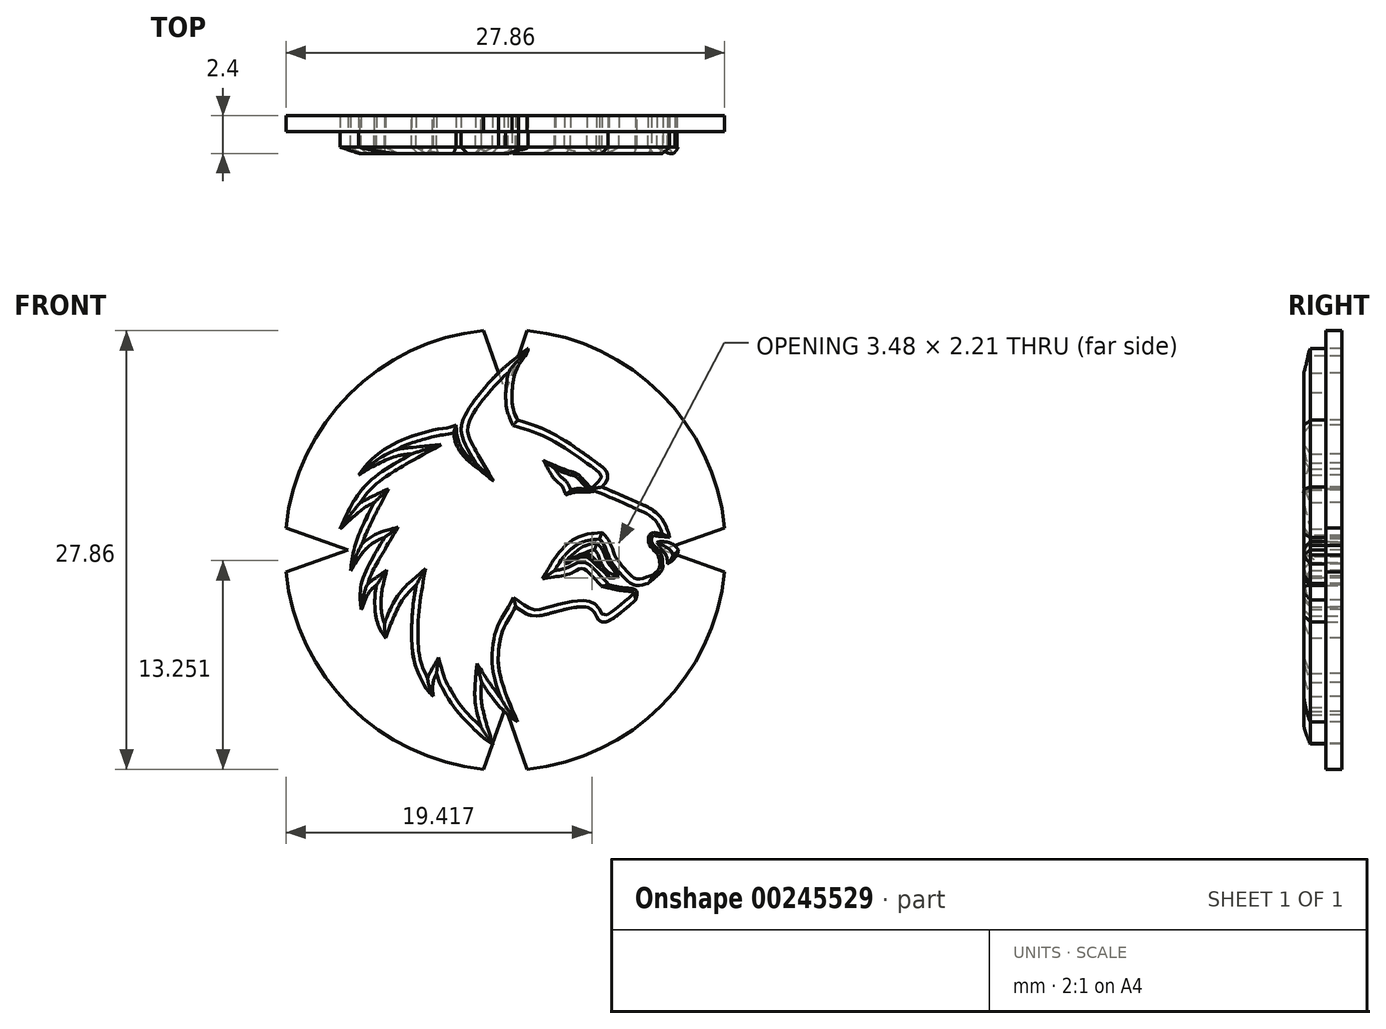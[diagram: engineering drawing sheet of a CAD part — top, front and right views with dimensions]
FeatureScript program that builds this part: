
annotation { "Feature Type Name" : "Feature", "Feature Type Description" : "" }
export const myFeature = defineFeature(function(context is Context, id is Id, definition is map)
    precondition{}
    {
        {
            var Q0;
            Q0=qCreatedBy(makeId("Front.planeOp"),FACE);
            var sketch = newSketch(context, id + "F0", { "sketchPlane" : qUnion([Q0])});
            skCircle(sketch, "E0", {"center": v(0, 0) * mm, "radius": 18 * mm, "construction": true});
            skCircle(sketch, "E1", {"center": v(0, 0) * mm, "radius": 17 * mm, "construction": true});
            skCircle(sketch, "E2", {"center": v(0, 0) * mm, "radius": 15 * mm, "construction": true});
            skLineSegment(sketch, "E3", {"start": v(-18, 18) * mm, "end": v(-18, -18) * mm, "construction": true});
            skLineSegment(sketch, "E4", {"start": v(-18, -18) * mm, "end": v(18, -18) * mm, "construction": true});
            skLineSegment(sketch, "E5", {"start": v(18, -18) * mm, "end": v(18, 18) * mm, "construction": true});
            skLineSegment(sketch, "E6", {"start": v(18, 18) * mm, "end": v(-18, 18) * mm, "construction": true});
            skFitSpline(sketch, "E7", {"points": [v(-10.49, 1.33) * mm, v(-9.43, 3.4) * mm, v(-8.08, 4.8) * mm, v(-5.95, 6.1) * mm], "startDerivative": vector(2.88, 6.53) * mm, "endDerivative": vector(6.47, 3.62) * mm});
            skFitSpline(sketch, "E8", {"points": [v(-9.32, 4.76) * mm, v(-8.35, 5.34) * mm, v(-6.9, 5.95) * mm, v(-5.95, 6.1) * mm], "startDerivative": vector(2.77, 1.79) * mm, "endDerivative": vector(3.02, 0.29) * mm});
            skFitSpline(sketch, "E9", {"points": [v(-3.13, 7.94) * mm, v(-3.48, 7.8) * mm, v(-4.26, 7.67) * mm, v(-5.45, 7.37) * mm, v(-6.65, 6.94) * mm, v(-7.65, 6.4) * mm, v(-8.6, 5.63) * mm, v(-9.32, 4.76) * mm], "startDerivative": vector(-3.58, -1.84) * mm, "endDerivative": vector(-4.37, -5.9) * mm});
            skFitSpline(sketch, "E10", {"points": [v(-1.9, 5.53) * mm, v(-2.35, 5.92) * mm, v(-2.78, 6.48) * mm, v(-3.04, 7.1) * mm, v(-3.13, 7.94) * mm], "startDerivative": vector(-1.97, 1.54) * mm, "endDerivative": vector(-0.18, 3.2) * mm});
            skFitSpline(sketch, "E11", {"points": [v(-8.33, 3.01) * mm, v(-8.87, 2.72) * mm, v(-9.58, 2.16) * mm, v(-10.49, 1.33) * mm], "startDerivative": vector(-1.95, -0.93) * mm, "endDerivative": vector(-2.37, -2.22) * mm});
            skFitSpline(sketch, "E12", {"points": [v(-9.83, -1.31) * mm, v(-9.69, -0.31) * mm, v(-9.39, 0.77) * mm, v(-8.9, 1.88) * mm, v(-8.33, 3.01) * mm], "startDerivative": vector(0.5, 4.23) * mm, "endDerivative": vector(2.2, 4.32) * mm});
            skFitSpline(sketch, "E13", {"points": [v(-7.67, 0.79) * mm, v(-8.05, 0.65) * mm, v(-8.65, 0.25) * mm, v(-9.12, -0.25) * mm, v(-9.83, -1.31) * mm], "startDerivative": vector(-1.94, -0.57) * mm, "endDerivative": vector(-2.32, -3.56) * mm});
            skFitSpline(sketch, "E14", {"points": [v(-9.15, -3.8) * mm, v(-9.22, -3.06) * mm, v(-9.1, -2) * mm, v(-8.5, -0.63) * mm, v(-7.67, 0.79) * mm], "startDerivative": vector(-0.5, 3.6) * mm, "endDerivative": vector(2.91, 4.84) * mm});
            skFitSpline(sketch, "E15", {"points": [v(-8.17, -2.23) * mm, v(-8.56, -2.55) * mm, v(-8.86, -3.09) * mm, v(-9.15, -3.8) * mm], "startDerivative": vector(-1.36, -0.97) * mm, "endDerivative": vector(-0.78, -1.96) * mm});
            skFitSpline(sketch, "E16", {"points": [v(-7.6, -5.6) * mm, v(-7.87, -5.2) * mm, v(-8.15, -4.51) * mm, v(-8.29, -3.61) * mm, v(-8.26, -2.67) * mm, v(-8.17, -2.23) * mm], "startDerivative": vector(-1.6, 2.21) * mm, "endDerivative": vector(0.59, 2.45) * mm});
            skFitSpline(sketch, "E17", {"points": [v(-5.66, -2.23) * mm, v(-6.13, -2.67) * mm, v(-6.67, -3.42) * mm, v(-7.18, -4.48) * mm, v(-7.6, -5.6) * mm], "startDerivative": vector(-2.28, -2) * mm, "endDerivative": vector(-1.47, -4.03) * mm});
            skFitSpline(sketch, "E18", {"points": [v(-4.57, -9.32) * mm, v(-4.99, -8.85) * mm, v(-5.45, -8.01) * mm, v(-5.86, -6.73) * mm, v(-5.95, -4.95) * mm, v(-5.86, -3.52) * mm, v(-5.66, -2.23) * mm], "startDerivative": vector(-3.52, 3.53) * mm, "endDerivative": vector(1.32, 7.43) * mm});
            skFitSpline(sketch, "E19", {"points": [v(-4.37, -7.85) * mm, v(-4.52, -8.18) * mm, v(-4.62, -8.75) * mm, v(-4.57, -9.32) * mm], "startDerivative": vector(-0.58, -1.04) * mm, "endDerivative": vector(0.22, -1.55) * mm});
            skFitSpline(sketch, "E20", {"points": [v(-0.79, -12.36) * mm, v(-1.46, -11.87) * mm, v(-2.24, -11.13) * mm, v(-3.13, -10.15) * mm, v(-3.75, -9.22) * mm, v(-4.15, -8.49) * mm, v(-4.37, -7.85) * mm], "startDerivative": vector(-4.36, 2.91) * mm, "endDerivative": vector(-1.35, 4.54) * mm});
            skFitSpline(sketch, "E21", {"points": [v(-1.51, -8.4) * mm, v(-1.54, -8.88) * mm, v(-1.52, -9.6) * mm, v(-1.37, -10.41) * mm, v(-1.1, -11.41) * mm, v(-0.79, -12.36) * mm], "startDerivative": vector(-0.24, -2.87) * mm, "endDerivative": vector(1.38, -4.16) * mm});
            skFitSpline(sketch, "E22", {"points": [v(0.78, -10.93) * mm, v(0.3, -10.6) * mm, v(-0.3, -10.03) * mm, v(-0.96, -9.22) * mm, v(-1.51, -8.4) * mm], "startDerivative": vector(-2.26, 1.48) * mm, "endDerivative": vector(-1.97, 3) * mm});
            skFitSpline(sketch, "E23", {"points": [v(0.66, -3.6) * mm, v(0.38, -4.1) * mm, v(-0.17, -5.12) * mm, v(-0.42, -6.39) * mm, v(-0.42, -7.5) * mm, v(0.07, -9.25) * mm, v(0.78, -10.93) * mm], "startDerivative": vector(-2.16, -4.03) * mm, "endDerivative": vector(3.61, -8.1) * mm});
            skFitSpline(sketch, "E24", {"points": [v(8.27, -3.19) * mm, v(6.84, -4.35) * mm, v(6.29, -4.58) * mm, v(5.92, -4.45) * mm, v(5.68, -4.04) * mm, v(5.38, -3.71) * mm, v(4.74, -3.62) * mm, v(3.17, -3.93) * mm, v(2.23, -4.17) * mm, v(1.52, -4.14) * mm, v(0.66, -3.6) * mm], "startDerivative": vector(-10.5, -9.12) * mm, "endDerivative": vector(-7.73, 5.86) * mm});
            skFitSpline(sketch, "E25", {"points": [v(6.58, -2.23) * mm, v(7.37, -2.39) * mm, v(8, -2.46) * mm, v(8.33, -2.62) * mm, v(8.27, -3.19) * mm], "startDerivative": vector(2.74, -0.65) * mm, "endDerivative": vector(-0.75, -2.68) * mm});
            skFitSpline(sketch, "E26", {"points": [v(3.13, -1.31) * mm, v(3.95, -1.14) * mm, v(4.38, -0.92) * mm, v(4.8, -0.78) * mm, v(5.26, -0.9) * mm, v(5.73, -1.31) * mm, v(6.58, -2.23) * mm], "startDerivative": vector(4.8, 0.73) * mm, "endDerivative": vector(3.99, -4.35) * mm});
            skFitSpline(sketch, "E27", {"points": [v(1.45, 12.8) * mm, v(0.94, 12.41) * mm, v(-0.34, 11.34) * mm, v(-1.27, 10.36) * mm, v(-2.2, 9.16) * mm, v(-2.7, 8.25) * mm, v(-2.8, 7.58) * mm, v(-2.59, 6.8) * mm, v(-1.9, 5.53) * mm], "startDerivative": vector(-4.66, -3.44) * mm, "endDerivative": vector(5.45, -9.26) * mm});
            skFitSpline(sketch, "E28", {"points": [v(0.78, 8.24) * mm, v(0.5, 8.98) * mm, v(0.43, 10.17) * mm, v(0.78, 11.63) * mm, v(1.38, 12.53) * mm, v(1.45, 12.8) * mm], "startDerivative": vector(-1.77, 3.71) * mm, "endDerivative": vector(0.21, 2.22) * mm});
            skFitSpline(sketch, "E29", {"points": [v(6.13, 4) * mm, v(6.43, 4.36) * mm, v(6.47, 4.88) * mm, v(5.82, 5.53) * mm, v(4.55, 6.42) * mm, v(3.45, 7.14) * mm, v(2.33, 7.72) * mm, v(0.78, 8.24) * mm], "startDerivative": vector(3.54, 3.42) * mm, "endDerivative": vector(-9.1, 2.77) * mm});
            skFitSpline(sketch, "E30", {"points": [v(3.18, 5.13) * mm, v(3.42, 4.76) * mm, v(3.68, 4.52) * mm, v(3.89, 4.32) * mm, v(4.03, 4.1) * mm, v(4.15, 3.8) * mm], "startDerivative": vector(0.95, -1.73) * mm, "endDerivative": vector(0.59, -1.54) * mm});
            skFitSpline(sketch, "E31", {"points": [v(5.2, 3.89) * mm, v(4.98, 4.14) * mm, v(4.79, 4.36) * mm, v(4.61, 4.53) * mm, v(4.4, 4.7) * mm, v(4.19, 4.76) * mm, v(3.81, 4.89) * mm, v(3.5, 5) * mm, v(3.18, 5.13) * mm], "startDerivative": vector(-1.64, 1.95) * mm, "endDerivative": vector(-2.38, 1.04) * mm});
            skFitSpline(sketch, "E32", {"points": [v(4.15, 3.8) * mm, v(4.4, 3.87) * mm, v(4.62, 3.9) * mm, v(4.85, 3.89) * mm, v(5.2, 3.89) * mm], "startDerivative": vector(1, 0.29) * mm, "endDerivative": vector(1.25, 0.03) * mm});
            skFitSpline(sketch, "E33", {"points": [v(10.44, 0.79) * mm, v(10.33, 1.18) * mm, v(10, 1.9) * mm, v(9.66, 2.29) * mm, v(9.23, 2.62) * mm, v(8.4, 3.01) * mm, v(7.17, 3.55) * mm, v(6.13, 4) * mm], "startDerivative": vector(-0.8, 3.45) * mm, "endDerivative": vector(-5.9, 2.46) * mm});
            skFitSpline(sketch, "E34", {"points": [v(3.13, -1.31) * mm, v(3.31, -1) * mm, v(3.74, -0.39) * mm, v(4.35, 0.19) * mm, v(5.03, 0.54) * mm, v(5.97, 0.69) * mm], "startDerivative": vector(1.16, 2.03) * mm, "endDerivative": vector(4.3, 0.39) * mm});
            skFitSpline(sketch, "E35", {"points": [v(9.07, -2.12) * mm, v(8.67, -2.23) * mm, v(8.18, -2.23) * mm, v(7.78, -1.97) * mm, v(7.35, -1.56) * mm, v(6.85, -0.93) * mm, v(6.64, -0.63) * mm, v(6.53, -0.35) * mm, v(6.34, 0.14) * mm, v(6.2, 0.43) * mm, v(5.97, 0.69) * mm], "startDerivative": vector(-3.96, -1.23) * mm, "endDerivative": vector(-2.8, 2.95) * mm});
            skFitSpline(sketch, "E36", {"points": [v(9.07, -2.12) * mm, v(9.38, -1.86) * mm, v(9.75, -1.5) * mm, v(9.96, -1.27) * mm, v(10, -0.95) * mm, v(9.93, -0.42) * mm, v(9.72, -0.05) * mm, v(9.5, 0.22) * mm, v(9.32, 0.44) * mm, v(9.27, 0.63) * mm, v(9.29, 0.79) * mm, v(9.37, 0.9) * mm, v(9.6, 0.89) * mm, v(10.44, 0.79) * mm], "startDerivative": vector(3.69, 2.83) * mm, "endDerivative": vector(7.96, -0.84) * mm});
            skFitSpline(sketch, "E37", {"points": [v(5.8, 0.43) * mm, v(5.97, 0.27) * mm, v(6.17, 0) * mm, v(6.34, -0.42) * mm, v(6.51, -0.77) * mm, v(6.8, -1.2) * mm, v(7.23, -1.64) * mm], "startDerivative": vector(1.64, -1.22) * mm, "endDerivative": vector(2.15, -2.15) * mm});
            skFitSpline(sketch, "E38", {"points": [v(6.58, -1.77) * mm, v(6.9, -1.77) * mm, v(7.23, -1.64) * mm], "startDerivative": vector(0.65, -0.06) * mm, "endDerivative": vector(0.64, 0.33) * mm});
            skFitSpline(sketch, "E39", {"points": [v(9.62, 0.48) * mm, v(9.82, 0.2) * mm, v(9.98, -0.06) * mm, v(10.12, -0.22) * mm, v(10.22, -0.37) * mm, v(10.28, -0.58) * mm, v(10.28, -0.88) * mm], "startDerivative": vector(1.09, -1.48) * mm, "endDerivative": vector(-0.04, -1.75) * mm});
            skFitSpline(sketch, "E40", {"points": [v(9.62, 0.48) * mm, v(9.76, 0.52) * mm, v(10.17, 0.5) * mm, v(10.65, 0.36) * mm, v(10.98, 0) * mm], "startDerivative": vector(0.77, 0.28) * mm, "endDerivative": vector(1.05, -1.4) * mm});
            skFitSpline(sketch, "E41", {"points": [v(10.28, -0.88) * mm, v(10.47, -0.78) * mm, v(10.7, -0.6) * mm, v(10.86, -0.37) * mm, v(10.95, -0.21) * mm, v(10.98, 0) * mm], "startDerivative": vector(0.96, 0.5) * mm, "endDerivative": vector(0.12, 1.19) * mm});
            skFitSpline(sketch, "E42", {"points": [v(3.75, -0.86) * mm, v(3.94, -0.84) * mm, v(4.22, -0.68) * mm, v(4.57, -0.52) * mm, v(4.9, -0.44) * mm, v(5.23, -0.49) * mm, v(5.51, -0.71) * mm, v(5.9, -1.07) * mm, v(6.2, -1.33) * mm, v(6.44, -1.6) * mm, v(6.58, -1.77) * mm], "startDerivative": vector(2.52, -0.03) * mm, "endDerivative": vector(1.67, -2) * mm});
            skFitSpline(sketch, "E43", {"points": [v(5.8, 0.43) * mm, v(5.46, 0.38) * mm, v(5.16, 0.29) * mm, v(4.77, 0.11) * mm, v(4.34, -0.23) * mm, v(3.98, -0.55) * mm, v(3.75, -0.86) * mm], "startDerivative": vector(-2.27, -0.23) * mm, "endDerivative": vector(-1.33, -1.97) * mm});
            skSolve(sketch);
        }
        {
            var Q0;
            Q0=qCreatedBy(makeId("Front.planeOp"),FACE);
            var sketch = newSketch(context, id + "F1", { "sketchPlane" : qUnion([Q0])});
            skCircle(sketch, "E44", {"center": v(0, 0) * mm, "radius": 20 * mm});
            skLineSegment(sketch, "E45", {"start": v(0, 25.78) * mm, "end": v(0, -27.28) * mm, "construction": true});
            skLineSegment(sketch, "E46", {"start": v(-28.3, 0) * mm, "end": v(31.37, 0) * mm, "construction": true});
            skLineSegment(sketch, "E47", {"start": v(-22, 0) * mm, "end": v(-16, 2.12) * mm});
            skLineSegment(sketch, "E48", {"start": v(-16, 2.12) * mm, "end": v(-10, 0) * mm});
            skLineSegment(sketch, "E49", {"start": v(-10, 0) * mm, "end": v(-16, -2.12) * mm});
            skLineSegment(sketch, "E50", {"start": v(-16, -2.12) * mm, "end": v(-22, 0) * mm});
            skLineSegment(sketch, "E51.0", {"start": v(-16, 1.06) * mm, "end": v(-13, 0) * mm});
            skLineSegment(sketch, "E51.1", {"start": v(-19, 0) * mm, "end": v(-16, 1.06) * mm});
            skLineSegment(sketch, "E51.2", {"start": v(-16, -1.06) * mm, "end": v(-19, 0) * mm});
            skLineSegment(sketch, "E51.3", {"start": v(-13, 0) * mm, "end": v(-16, -1.06) * mm});
            skCircle(sketch, "E52", {"center": v(0, 0) * mm, "radius": 14 * mm});
            skLineSegment(sketch, "E53", {"start": v(-23.43, 23.43) * mm, "end": v(21.13, -21.13) * mm, "construction": true});
            skLineSegment(sketch, "E54.MirrorCS", {"start": v(10, 0) * mm, "end": v(16, -2.12) * mm});
            skLineSegment(sketch, "E55.MirrorCS", {"start": v(13, 0) * mm, "end": v(16, -1.06) * mm});
            skLineSegment(sketch, "E56.MirrorCS", {"start": v(16, -1.06) * mm, "end": v(19, 0) * mm});
            skLineSegment(sketch, "E57.MirrorCS", {"start": v(16, -2.12) * mm, "end": v(22, 0) * mm});
            skLineSegment(sketch, "E58.MirrorCS", {"start": v(22, 0) * mm, "end": v(16, 2.12) * mm});
            skLineSegment(sketch, "E59.MirrorCS", {"start": v(16, 2.12) * mm, "end": v(10, 0) * mm});
            skLineSegment(sketch, "E60.MirrorCS", {"start": v(16, 1.06) * mm, "end": v(13, 0) * mm});
            skLineSegment(sketch, "E61.MirrorCS", {"start": v(19, 0) * mm, "end": v(16, 1.06) * mm});
            skLineSegment(sketch, "E62.MirrorCS", {"start": v(0, 19) * mm, "end": v(-1.06, 16) * mm});
            skLineSegment(sketch, "E63.MirrorCS", {"start": v(1.06, 16) * mm, "end": v(0, 19) * mm});
            skLineSegment(sketch, "E64.MirrorCS", {"start": v(0, 22) * mm, "end": v(-2.12, 16) * mm});
            skLineSegment(sketch, "E65.MirrorCS", {"start": v(2.12, 16) * mm, "end": v(0, 22) * mm});
            skLineSegment(sketch, "E66.MirrorCS", {"start": v(0, 10) * mm, "end": v(2.12, 16) * mm});
            skLineSegment(sketch, "E67.MirrorCS", {"start": v(0, 13) * mm, "end": v(1.06, 16) * mm});
            skLineSegment(sketch, "E68.MirrorCS", {"start": v(-1.06, 16) * mm, "end": v(0, 13) * mm});
            skLineSegment(sketch, "E69.MirrorCS", {"start": v(-2.12, 16) * mm, "end": v(0, 10) * mm});
            skLineSegment(sketch, "E70.MirrorCS", {"start": v(0, -10) * mm, "end": v(2.12, -16) * mm});
            skLineSegment(sketch, "E71.MirrorCS", {"start": v(0, -13) * mm, "end": v(1.06, -16) * mm});
            skLineSegment(sketch, "E72.MirrorCS", {"start": v(-1.06, -16) * mm, "end": v(0, -13) * mm});
            skLineSegment(sketch, "E73.MirrorCS", {"start": v(-2.12, -16) * mm, "end": v(0, -10) * mm});
            skLineSegment(sketch, "E74.MirrorCS", {"start": v(0, -22) * mm, "end": v(-2.12, -16) * mm});
            skLineSegment(sketch, "E75.MirrorCS", {"start": v(0, -19) * mm, "end": v(-1.06, -16) * mm});
            skLineSegment(sketch, "E76.MirrorCS", {"start": v(1.06, -16) * mm, "end": v(0, -19) * mm});
            skLineSegment(sketch, "E77.MirrorCS", {"start": v(2.12, -16) * mm, "end": v(0, -22) * mm});
            skSolve(sketch);
        }
        {
            var Q0;
            {var subQ12=sQuery(id+"F1.wireOp",EDGE,"E48");var subQ14=sQuery(id+"F1.wireOp",EDGE,"E49");var subQ18=makeQuery(id+"F1.imprint","INTERSECT",VERTEX,{"derivedFrom":[subQ12,subQ14]});Q0=makeQuery(id+"F1.imprint","IMPRINT",FACE,{"disambiguationData":[TD([[makeQuery(id+"F1.imprint","IMPRINT",EDGE,{"disambiguationData":[TD([[subQ18,1.0]])],"derivedFrom":subQ12}),1.0]])]});}
            extrude(context, id + "F2", {"entities" : qUnion([Q0]), "oppositeDirection" : true, "depth" : 1 * mm});
        }
        {
            var Q0;
            Q0=makeQuery(id+"F0.imprint","IMPRINT",FACE,{"disambiguationData":[TD([[makeQuery(id+"F0.imprint","IMPRINT",EDGE,{"derivedFrom":sQuery(id+"F0.wireOp",EDGE,"E7")}),-1.0]])]});
            var Q1;
            Q1=makeQuery(id+"F0.imprint","IMPRINT",FACE,{"disambiguationData":[TD([[makeQuery(id+"F0.imprint","IMPRINT",EDGE,{"derivedFrom":sQuery(id+"F0.wireOp",EDGE,"e38c4cf1-d7ad-4980-8dd1-fedaf0ec52b0")}),-1.0]])]});
            var Q2;
            Q2=makeQuery(id+"F0.imprint","IMPRINT",FACE,{"disambiguationData":[TD([[makeQuery(id+"F0.imprint","IMPRINT",EDGE,{"derivedFrom":sQuery(id+"F0.wireOp",EDGE,"E39")}),1.0]])]});
            var Q3;
            Q3=makeQuery(id+"F0.imprint","IMPRINT",FACE,{"disambiguationData":[TD([[makeQuery(id+"F0.imprint","IMPRINT",EDGE,{"derivedFrom":sQuery(id+"F0.wireOp",EDGE,"E37")}),-1.0]])]});
            extrude(context, id + "F3", {"entities" : qUnion([Q0, Q1, Q2, Q3]), "operationType" : NewBodyOperationType.REMOVE, "oppositeDirection" : true, "depth" : 1 * mm});
        }
        {
            var Q0;
            Q0 = qSketchRegion(id + "F0", true);
            extrude(context, id + "F4", {"entities" : qUnion([Q0]), "depth" : 1.4 * mm});
        }
        {
            var Q0;
            Q0=makeQuery(id+"F4.opExtrude","CAP_EDGE",EDGE,{"disambiguationData":[OSD([sQuery(id+"F0.wireOp",EDGE,"E23")])],"isStart":false});
            var Q1;
            Q1=makeQuery(id+"F4.opExtrude","CAP_EDGE",EDGE,{"disambiguationData":[OSD([sQuery(id+"F0.wireOp",EDGE,"E24")])],"isStart":false});
            var Q2;
            Q2=makeQuery(id+"F4.opExtrude","CAP_EDGE",EDGE,{"disambiguationData":[OSD([sQuery(id+"F0.wireOp",EDGE,"E22")])],"isStart":false});
            var Q3;
            Q3=makeQuery(id+"F4.opExtrude","CAP_EDGE",EDGE,{"disambiguationData":[OSD([sQuery(id+"F0.wireOp",EDGE,"E21")])],"isStart":false});
            var Q4;
            Q4=makeQuery(id+"F4.opExtrude","CAP_EDGE",EDGE,{"disambiguationData":[OSD([sQuery(id+"F0.wireOp",EDGE,"E20")])],"isStart":false});
            var Q5;
            Q5=makeQuery(id+"F4.opExtrude","CAP_EDGE",EDGE,{"disambiguationData":[OSD([sQuery(id+"F0.wireOp",EDGE,"E19")])],"isStart":false});
            var Q6;
            Q6=makeQuery(id+"F4.opExtrude","CAP_EDGE",EDGE,{"disambiguationData":[OSD([sQuery(id+"F0.wireOp",EDGE,"E18")])],"isStart":false});
            var Q7;
            Q7=makeQuery(id+"F4.opExtrude","CAP_EDGE",EDGE,{"disambiguationData":[OSD([sQuery(id+"F0.wireOp",EDGE,"E17")])],"isStart":false});
            var Q8;
            Q8=makeQuery(id+"F4.opExtrude","CAP_EDGE",EDGE,{"disambiguationData":[OSD([sQuery(id+"F0.wireOp",EDGE,"E16")])],"isStart":false});
            var Q9;
            Q9=makeQuery(id+"F4.opExtrude","CAP_EDGE",EDGE,{"disambiguationData":[OSD([sQuery(id+"F0.wireOp",EDGE,"E15")])],"isStart":false});
            var Q10;
            Q10=makeQuery(id+"F4.opExtrude","CAP_EDGE",EDGE,{"disambiguationData":[OSD([sQuery(id+"F0.wireOp",EDGE,"E14")])],"isStart":false});
            var Q11;
            Q11=makeQuery(id+"F4.opExtrude","CAP_EDGE",EDGE,{"disambiguationData":[OSD([sQuery(id+"F0.wireOp",EDGE,"E13")])],"isStart":false});
            var Q12;
            Q12=makeQuery(id+"F4.opExtrude","CAP_EDGE",EDGE,{"disambiguationData":[OSD([sQuery(id+"F0.wireOp",EDGE,"E12")])],"isStart":false});
            var Q13;
            Q13=makeQuery(id+"F4.opExtrude","CAP_EDGE",EDGE,{"disambiguationData":[OSD([sQuery(id+"F0.wireOp",EDGE,"E11")])],"isStart":false});
            var Q14;
            Q14=makeQuery(id+"F4.opExtrude","CAP_EDGE",EDGE,{"disambiguationData":[OSD([sQuery(id+"F0.wireOp",EDGE,"E7")])],"isStart":false});
            var Q15;
            Q15=makeQuery(id+"F4.opExtrude","CAP_EDGE",EDGE,{"disambiguationData":[OSD([sQuery(id+"F0.wireOp",EDGE,"E8")])],"isStart":false});
            var Q16;
            Q16=makeQuery(id+"F4.opExtrude","CAP_EDGE",EDGE,{"disambiguationData":[OSD([sQuery(id+"F0.wireOp",EDGE,"E9")])],"isStart":false});
            var Q17;
            Q17=makeQuery(id+"F4.opExtrude","CAP_EDGE",EDGE,{"disambiguationData":[OSD([sQuery(id+"F0.wireOp",EDGE,"E27")])],"isStart":false});
            var Q18;
            Q18=makeQuery(id+"F4.opExtrude","CAP_EDGE",EDGE,{"disambiguationData":[OSD([sQuery(id+"F0.wireOp",EDGE,"E28")])],"isStart":false});
            var Q19;
            Q19=makeQuery(id+"F4.opExtrude","CAP_EDGE",EDGE,{"disambiguationData":[OSD([sQuery(id+"F0.wireOp",EDGE,"E29")])],"isStart":false});
            var Q20;
            Q20=makeQuery(id+"F4.opExtrude","CAP_EDGE",EDGE,{"disambiguationData":[OSD([sQuery(id+"F0.wireOp",EDGE,"E30")])],"isStart":false});
            var Q21;
            Q21=makeQuery(id+"F4.opExtrude","CAP_EDGE",EDGE,{"disambiguationData":[OSD([sQuery(id+"F0.wireOp",EDGE,"E33")])],"isStart":false});
            var Q22;
            Q22=makeQuery(id+"F4.opExtrude","CAP_EDGE",EDGE,{"disambiguationData":[OSD([sQuery(id+"F0.wireOp",EDGE,"E40")])],"isStart":false});
            var Q23;
            Q23=makeQuery(id+"F4.opExtrude","CAP_EDGE",EDGE,{"disambiguationData":[OSD([sQuery(id+"F0.wireOp",EDGE,"E39")])],"isStart":false});
            var Q24;
            Q24=makeQuery(id+"F4.opExtrude","CAP_EDGE",EDGE,{"disambiguationData":[OSD([sQuery(id+"F0.wireOp",EDGE,"E35")])],"isStart":false});
            var Q25;
            Q25=makeQuery(id+"F4.opExtrude","CAP_EDGE",EDGE,{"disambiguationData":[OSD([sQuery(id+"F0.wireOp",EDGE,"E34")])],"isStart":false});
            var Q26;
            Q26=makeQuery(id+"F4.opExtrude","CAP_EDGE",EDGE,{"disambiguationData":[OSD([sQuery(id+"F0.wireOp",EDGE,"E26")])],"isStart":false});
            var Q27;
            Q27=makeQuery(id+"F4.opExtrude","CAP_EDGE",EDGE,{"disambiguationData":[OSD([sQuery(id+"F0.wireOp",EDGE,"E37")])],"isStart":false});
            var Q28;
            Q28=makeQuery(id+"F4.opExtrude","CAP_EDGE",EDGE,{"disambiguationData":[OSD([sQuery(id+"F0.wireOp",EDGE,"E38")])],"isStart":false});
            var Q29;
            Q29=makeQuery(id+"F4.opExtrude","CAP_EDGE",EDGE,{"disambiguationData":[OSD([sQuery(id+"F0.wireOp",EDGE,"E43")])],"isStart":false});
            chamfer(context, id + "F5", {"entities" : qUnion([Q0, Q1, Q2, Q3, Q4, Q5, Q6, Q7, Q8, Q9, Q10, Q11, Q12, Q13, Q14, Q15, Q16, Q17, Q18, Q19, Q20, Q21, Q22, Q23, Q24, Q25, Q26, Q27, Q28, Q29]), "width" : 0.4 * mm, "tangentPropagation" : true});
        }
        {
            var Q0;
            Q0=makeQuery(id+"F4.opExtrude","CAP_EDGE",EDGE,{"disambiguationData":[OSD([sQuery(id+"F0.wireOp",EDGE,"E41")])],"isStart":false});
            var Q1;
            Q1=makeQuery(id+"F4.opExtrude","CAP_EDGE",EDGE,{"disambiguationData":[OSD([sQuery(id+"F0.wireOp",EDGE,"E10")])],"isStart":false});
            var Q2;
            Q2=makeQuery(id+"F4.opExtrude","CAP_EDGE",EDGE,{"disambiguationData":[OSD([sQuery(id+"F0.wireOp",EDGE,"E42")])],"isStart":false});
            chamfer(context, id + "F6", {"entities" : qUnion([Q0, Q1, Q2]), "chamferType" : ChamferType.TWO_OFFSETS, "width1" : 0.4 * mm, "oppositeDirection" : true, "width2" : 0.2 * mm, "tangentPropagation" : true});
        }
        {
            var Q0;
            Q0=makeQuery(id+"F4.opExtrude","CAP_EDGE",EDGE,{"disambiguationData":[OSD([sQuery(id+"F0.wireOp",EDGE,"E31")])],"isStart":false});
            var Q1;
            Q1=makeQuery(id+"F4.opExtrude","CAP_EDGE",EDGE,{"disambiguationData":[OSD([sQuery(id+"F0.wireOp",EDGE,"E32")])],"isStart":false});
            chamfer(context, id + "F7", {"entities" : qUnion([Q0, Q1]), "chamferType" : ChamferType.TWO_OFFSETS, "width1" : 0.4 * mm, "oppositeDirection" : false, "width2" : 0.2 * mm, "tangentPropagation" : true});
        }
        {
            var Q0;
            Q0=makeQuery(id+"F4.opExtrude","CAP_EDGE",EDGE,{"disambiguationData":[OSD([sQuery(id+"F0.wireOp",EDGE,"E25")])],"isStart":false});
            var Q1;
            Q1=makeQuery(id+"F4.opExtrude","CAP_EDGE",EDGE,{"disambiguationData":[OSD([sQuery(id+"F0.wireOp",EDGE,"E36")])],"isStart":false});
            chamfer(context, id + "F8", {"entities" : qUnion([Q0, Q1]), "chamferType" : ChamferType.TWO_OFFSETS, "width1" : 0.4 * mm, "oppositeDirection" : false, "width2" : 0.19 * mm, "tangentPropagation" : true});
        }
        {
            var Q0;
            {var subQ3=sQuery(id+"F1.wireOp",EDGE,"E52");var subQ6=sQuery(id+"F1.wireOp",EDGE,"E66.MirrorCS");var subQ8=makeQuery(id+"F1.imprint","INTERSECT",VERTEX,{"derivedFrom":[subQ3,subQ6]});Q0=makeQuery(id+"F1.imprint","IMPRINT",FACE,{"disambiguationData":[TD([[makeQuery(id+"F1.imprint","IMPRINT",EDGE,{"disambiguationData":[TD([[subQ8,-1.0]])],"derivedFrom":subQ3}),1.0]])]});}
            var Q1;
            {var subQ3=sQuery(id+"F1.wireOp",EDGE,"E52");var subQ5=sQuery(id+"F1.wireOp",EDGE,"E59.MirrorCS");var subQ10=makeQuery(id+"F1.imprint","INTERSECT",VERTEX,{"derivedFrom":[subQ3,subQ5]});Q1=makeQuery(id+"F1.imprint","IMPRINT",FACE,{"disambiguationData":[TD([[makeQuery(id+"F1.imprint","IMPRINT",EDGE,{"disambiguationData":[TD([[subQ10,1.0]])],"derivedFrom":subQ3}),1.0]])]});}
            var Q2;
            {var subQ3=sQuery(id+"F1.wireOp",EDGE,"E52");var subQ5=sQuery(id+"F1.wireOp",EDGE,"E73.MirrorCS");var subQ9=makeQuery(id+"F1.imprint","INTERSECT",VERTEX,{"derivedFrom":[subQ3,subQ5]});Q2=makeQuery(id+"F1.imprint","IMPRINT",FACE,{"disambiguationData":[TD([[makeQuery(id+"F1.imprint","IMPRINT",EDGE,{"disambiguationData":[TD([[subQ9,-1.0]])],"derivedFrom":subQ3}),1.0]])]});}
            extrude(context, id + "F9", {"entities" : qUnion([Q0, Q1, Q2]), "operationType" : NewBodyOperationType.REMOVE, "depth" : 1 * mm});
        }
    });
